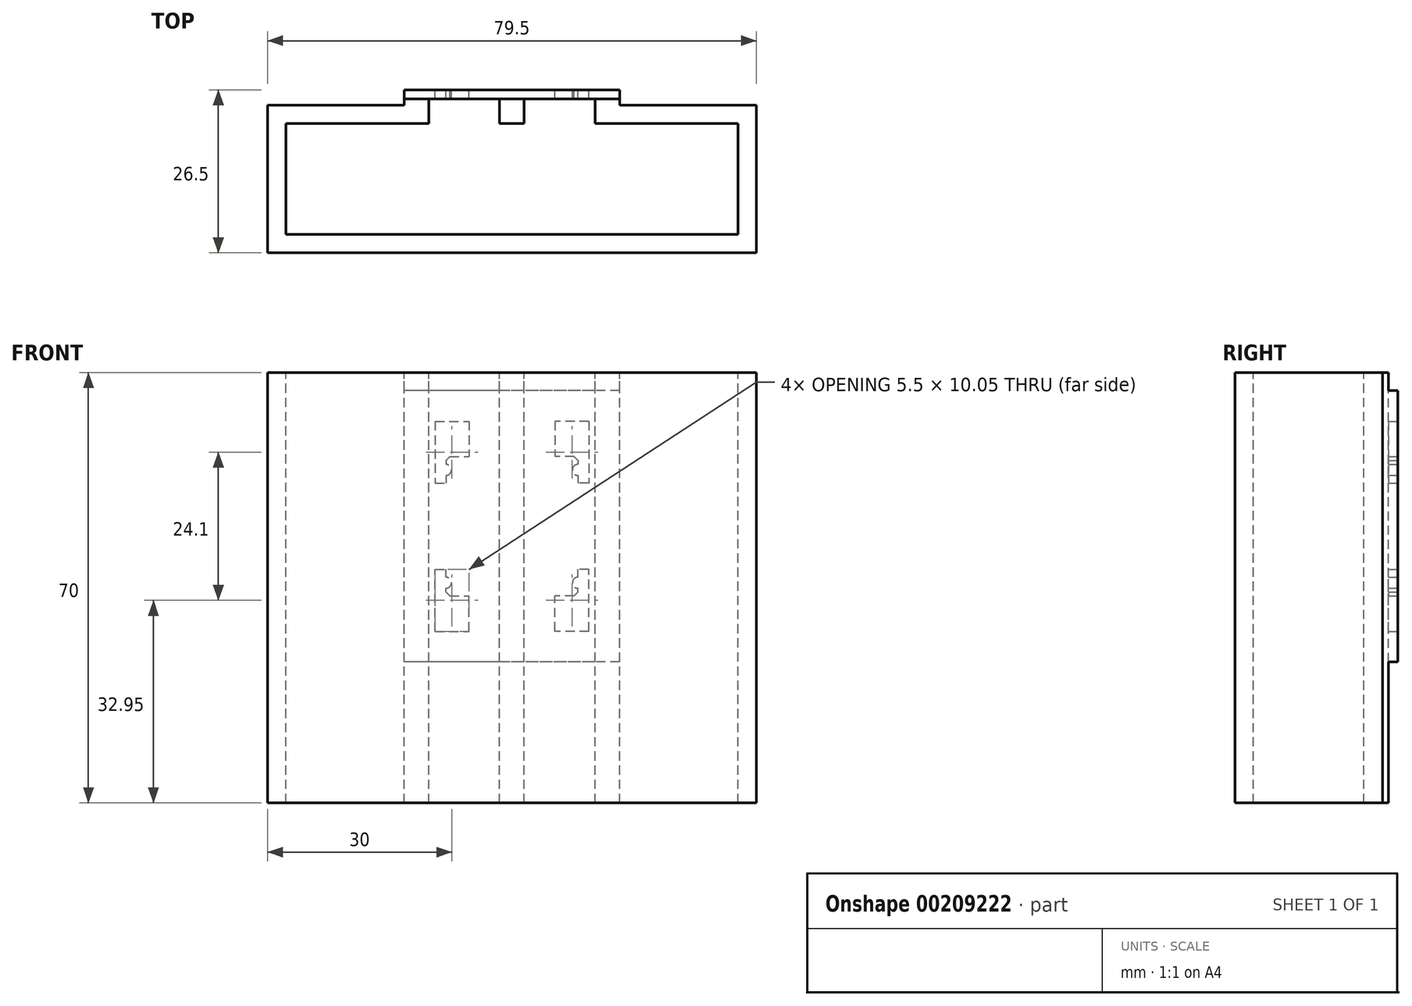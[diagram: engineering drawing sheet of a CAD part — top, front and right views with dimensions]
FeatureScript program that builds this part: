
annotation { "Feature Type Name" : "Feature", "Feature Type Description" : "" }
export const myFeature = defineFeature(function(context is Context, id is Id, definition is map)
    precondition{}
    {
        {
            var Q0;
            Q0=qCreatedBy(makeId("Front.planeOp"),FACE);
            var sketch = newSketch(context, id + "F0", { "sketchPlane" : qUnion([Q0])});
            skLineSegment(sketch, "E0", {"start": v(-12.5, 0) * mm, "end": v(12.5, 0) * mm, "construction": true});
            skLineSegment(sketch, "E1", {"start": v(0, 17.07) * mm, "end": v(0, -17.07) * mm, "construction": true});
            skLineSegment(sketch, "E2.bottom", {"start": v(12.5, 17.07) * mm, "end": v(-12.5, 17.07) * mm, "construction": true});
            skLineSegment(sketch, "E2.top", {"start": v(12.5, -17.07) * mm, "end": v(-12.5, -17.07) * mm, "construction": true});
            skLineSegment(sketch, "E2.left", {"start": v(12.5, 17.07) * mm, "end": v(12.5, -17.07) * mm, "construction": true});
            skLineSegment(sketch, "E2.right", {"start": v(-12.5, 17.07) * mm, "end": v(-12.5, -17.07) * mm, "construction": true});
            skPoint(sketch, "E2.middle", {"position": v(0, 0) * mm});
            skLineSegment(sketch, "E3.bottom", {"start": v(12.5, 17.07) * mm, "end": v(7, 17.07) * mm});
            skLineSegment(sketch, "E3.top", {"start": v(10.13, 11.32) * mm, "end": v(7, 11.32) * mm});
            skLineSegment(sketch, "E3.left", {"start": v(12.5, 17.07) * mm, "end": v(12.5, 11.32) * mm});
            skLineSegment(sketch, "E3.right", {"start": v(7, 17.07) * mm, "end": v(7, 11.32) * mm});
            skLineSegment(sketch, "E4.top", {"start": v(12.5, 7.03) * mm, "end": v(10.75, 7.03) * mm});
            skLineSegment(sketch, "E4.left", {"start": v(12.5, 11.32) * mm, "end": v(12.5, 7.03) * mm});
            skLineSegment(sketch, "E4.right", {"start": v(10.75, 10.7) * mm, "end": v(10.75, 10.08) * mm});
            skArc(sketch, "E5", {"start": v(10.75, 10.07) * mm, "mid": v(9.85, 9.17) * mm, "end": v(10.75, 8.27) * mm});
            skLineSegment(sketch, "E6.trimOffspring", {"start": v(10.75, 8.28) * mm, "end": v(10.75, 7.03) * mm});
            skLineSegment(sketch, "E7", {"start": v(10.75, 10.7) * mm, "end": v(10.13, 11.32) * mm});
            skPoint(sketch, "E8.orphan", {"position": v(10.75, 11.32) * mm});
            skLineSegment(sketch, "E9.MirrorCS", {"start": v(-7, 17.07) * mm, "end": v(-7, 11.32) * mm});
            skLineSegment(sketch, "E10.MirrorCS", {"start": v(-12.5, 17.07) * mm, "end": v(-7, 17.07) * mm});
            skLineSegment(sketch, "E11.MirrorCS", {"start": v(-12.5, 17.07) * mm, "end": v(-12.5, 11.32) * mm});
            skLineSegment(sketch, "E12.MirrorCS", {"start": v(-12.5, 11.32) * mm, "end": v(-12.5, 7.02) * mm});
            skLineSegment(sketch, "E13.MirrorCS", {"start": v(-12.5, 7.02) * mm, "end": v(-10.75, 7.02) * mm});
            skLineSegment(sketch, "E14.MirrorCS", {"start": v(-10.75, 8.28) * mm, "end": v(-10.75, 7.03) * mm});
            skArc(sketch, "E15.MirrorCS", {"start": v(-10.75, 10.07) * mm, "mid": v(-9.85, 9.17) * mm, "end": v(-10.75, 8.27) * mm});
            skLineSegment(sketch, "E16.MirrorCS", {"start": v(-10.75, 10.7) * mm, "end": v(-10.75, 10.08) * mm});
            skLineSegment(sketch, "E17.MirrorCS", {"start": v(-10.75, 10.7) * mm, "end": v(-10.13, 11.32) * mm});
            skLineSegment(sketch, "E18.MirrorCS", {"start": v(-10.13, 11.32) * mm, "end": v(-7, 11.32) * mm});
            skLineSegment(sketch, "E19.MirrorCS", {"start": v(-10.75, -10.7) * mm, "end": v(-10.75, -10.08) * mm});
            skLineSegment(sketch, "E20.MirrorCS", {"start": v(10.75, -10.7) * mm, "end": v(10.75, -10.07) * mm});
            skLineSegment(sketch, "E21.MirrorCS", {"start": v(10.75, -10.7) * mm, "end": v(10.13, -11.32) * mm});
            skLineSegment(sketch, "E22.MirrorCS", {"start": v(-12.5, -7.03) * mm, "end": v(-10.75, -7.03) * mm});
            skLineSegment(sketch, "E23.MirrorCS", {"start": v(-10.75, -10.7) * mm, "end": v(-10.12, -11.33) * mm});
            skLineSegment(sketch, "E24.MirrorCS", {"start": v(-10.75, -8.28) * mm, "end": v(-10.75, -7.03) * mm});
            skLineSegment(sketch, "E25.MirrorCS", {"start": v(12.5, -7.02) * mm, "end": v(10.75, -7.02) * mm});
            skLineSegment(sketch, "E26.MirrorCS", {"start": v(10.75, -8.27) * mm, "end": v(10.75, -7.02) * mm});
            skLineSegment(sketch, "E27.MirrorCS", {"start": v(-7, -17.07) * mm, "end": v(-7, -11.32) * mm});
            skLineSegment(sketch, "E28.MirrorCS", {"start": v(-12.5, -17.07) * mm, "end": v(-12.5, -11.32) * mm});
            skArc(sketch, "E29.MirrorCS", {"start": v(-10.75, -10.08) * mm, "mid": v(-9.85, -9.17) * mm, "end": v(-10.75, -8.28) * mm});
            skLineSegment(sketch, "E30.MirrorCS", {"start": v(-10.13, -11.32) * mm, "end": v(-7, -11.32) * mm});
            skLineSegment(sketch, "E31.MirrorCS", {"start": v(12.5, -11.32) * mm, "end": v(12.5, -7.02) * mm});
            skLineSegment(sketch, "E32.MirrorCS", {"start": v(12.5, -17.07) * mm, "end": v(12.5, 17.07) * mm, "construction": true});
            skLineSegment(sketch, "E33.MirrorCS", {"start": v(12.5, -17.07) * mm, "end": v(12.5, -11.32) * mm});
            skLineSegment(sketch, "E34.MirrorCS", {"start": v(-12.5, -17.07) * mm, "end": v(-12.5, 17.07) * mm, "construction": true});
            skLineSegment(sketch, "E35.MirrorCS", {"start": v(0, -17.07) * mm, "end": v(0, 17.07) * mm, "construction": true});
            skPoint(sketch, "E36.MirrorP", {"position": v(10.75, -11.32) * mm});
            skLineSegment(sketch, "E37.MirrorCS", {"start": v(7, -17.07) * mm, "end": v(7, -11.32) * mm});
            skLineSegment(sketch, "E38.MirrorCS", {"start": v(-12.5, -17.07) * mm, "end": v(-7, -17.07) * mm});
            skArc(sketch, "E39.MirrorCS", {"start": v(10.75, -10.07) * mm, "mid": v(9.85, -9.17) * mm, "end": v(10.75, -8.27) * mm});
            skLineSegment(sketch, "E40.MirrorCS", {"start": v(-12.5, -11.32) * mm, "end": v(-12.5, -7.03) * mm});
            skLineSegment(sketch, "E41.MirrorCS", {"start": v(12.5, -17.07) * mm, "end": v(7, -17.07) * mm});
            skLineSegment(sketch, "E42.MirrorCS", {"start": v(10.13, -11.32) * mm, "end": v(7, -11.32) * mm});
            skLineSegment(sketch, "E43.0", {"start": v(17.5, 22.07) * mm, "end": v(-17.5, 22.07) * mm});
            skLineSegment(sketch, "E43.1", {"start": v(17.5, -22.07) * mm, "end": v(17.5, 22.07) * mm});
            skLineSegment(sketch, "E43.2", {"start": v(17.5, -22.07) * mm, "end": v(-17.5, -22.08) * mm});
            skLineSegment(sketch, "E43.3", {"start": v(-17.5, -22.08) * mm, "end": v(-17.5, 22.07) * mm});
            skSolve(sketch);
        }
        {
            var Q0;
            Q0=makeQuery(id+"F0.imprint","IMPRINT",FACE,{"disambiguationData":[TD([[makeQuery(id+"F0.imprint","IMPRINT",EDGE,{"derivedFrom":sQuery(id+"F0.wireOp",EDGE,"E3.bottom")}),-1.0]])]});
            extrude(context, id + "F1", {"entities" : qUnion([Q0]), "depth" : 1.5 * mm});
        }
        {
            var Q0;
            Q0=qCreatedBy(makeId("Top.planeOp"),FACE);
            var sketch = newSketch(context, id + "F2", { "sketchPlane" : qUnion([Q0])});
            skLineSegment(sketch, "E44", {"start": v(0, -5.5) * mm, "end": v(0, -23.5) * mm, "construction": true});
            skLineSegment(sketch, "E45", {"start": v(0, -23.5) * mm, "end": v(-36.75, -23.5) * mm, "construction": true});
            skLineSegment(sketch, "E46", {"start": v(-36.75, -23.5) * mm, "end": v(-36.75, -5.5) * mm, "construction": true});
            skLineSegment(sketch, "E47", {"start": v(-36.75, -5.5) * mm, "end": v(0, -5.5) * mm, "construction": true});
            skLineSegment(sketch, "E48", {"start": v(0, -5.5) * mm, "end": v(36.75, -5.5) * mm, "construction": true});
            skLineSegment(sketch, "E49", {"start": v(36.75, -5.5) * mm, "end": v(36.75, -23.5) * mm, "construction": true});
            skLineSegment(sketch, "E50", {"start": v(36.75, -23.5) * mm, "end": v(0, -23.5) * mm, "construction": true});
            skPoint(sketch, "E51", {"position": v(-17.5, -1.5) * mm});
            skPoint(sketch, "E52", {"position": v(17.5, -1.5) * mm});
            skLineSegment(sketch, "E53.bottom", {"start": v(-17.5, -1.5) * mm, "end": v(-13.5, -1.5) * mm});
            skLineSegment(sketch, "E53.top", {"start": v(-17.5, -5.5) * mm, "end": v(-13.5, -5.5) * mm});
            skLineSegment(sketch, "E53.left", {"start": v(-17.5, -1.5) * mm, "end": v(-17.5, -5.5) * mm});
            skLineSegment(sketch, "E53.right", {"start": v(-13.5, -1.5) * mm, "end": v(-13.5, -5.5) * mm});
            skLineSegment(sketch, "E54.bottom", {"start": v(17.5, -1.5) * mm, "end": v(13.5, -1.5) * mm});
            skLineSegment(sketch, "E54.top", {"start": v(17.5, -5.5) * mm, "end": v(13.5, -5.5) * mm});
            skLineSegment(sketch, "E54.left", {"start": v(17.5, -1.5) * mm, "end": v(17.5, -5.5) * mm});
            skLineSegment(sketch, "E54.right", {"start": v(13.5, -1.5) * mm, "end": v(13.5, -5.5) * mm});
            skLineSegment(sketch, "E55.bottom", {"start": v(-2, -5.5) * mm, "end": v(0, -5.5) * mm});
            skLineSegment(sketch, "E55.top", {"start": v(-2, -1.5) * mm, "end": v(0, -1.5) * mm});
            skLineSegment(sketch, "E55.left", {"start": v(-2, -5.5) * mm, "end": v(-2, -1.5) * mm});
            skLineSegment(sketch, "E56.bottom", {"start": v(0, -1.5) * mm, "end": v(2, -1.5) * mm});
            skLineSegment(sketch, "E56.top", {"start": v(0, -5.5) * mm, "end": v(2, -5.5) * mm});
            skLineSegment(sketch, "E56.right", {"start": v(2, -1.5) * mm, "end": v(2, -5.5) * mm});
            skLineSegment(sketch, "E57", {"start": v(17.5, -5.5) * mm, "end": v(36.75, -5.5) * mm});
            skLineSegment(sketch, "E58", {"start": v(36.75, -23.5) * mm, "end": v(-36.75, -23.5) * mm});
            skLineSegment(sketch, "E59", {"start": v(-36.75, -5.5) * mm, "end": v(-36.75, -23.5) * mm});
            skLineSegment(sketch, "E60", {"start": v(-36.75, -5.5) * mm, "end": v(-17.5, -5.5) * mm});
            skLineSegment(sketch, "E61", {"start": v(36.75, -5.5) * mm, "end": v(36.75, -23.5) * mm});
            skLineSegment(sketch, "E62", {"start": v(39.75, -2.5) * mm, "end": v(39.75, -26.5) * mm});
            skLineSegment(sketch, "E63", {"start": v(39.75, -26.5) * mm, "end": v(-39.75, -26.5) * mm});
            skLineSegment(sketch, "E64", {"start": v(-39.75, -26.5) * mm, "end": v(-39.75, -2.5) * mm});
            skLineSegment(sketch, "E65", {"start": v(-39.75, -2.5) * mm, "end": v(-17.5, -2.5) * mm});
            skLineSegment(sketch, "E66", {"start": v(39.75, -2.5) * mm, "end": v(17.5, -2.5) * mm});
            skSolve(sketch);
        }
        {
            var Q0;
            Q0 = qSketchRegion(id + "F2", true);
            extrude(context, id + "F3", {"entities" : qUnion([Q0]), "operationType" : NewBodyOperationType.ADD, "oppositeDirection" : true, "depth" : 45 * mm, "hasSecondDirection" : true, "secondDirectionOppositeDirection" : false, "secondDirectionDepth" : 25 * mm});
        }
    });
